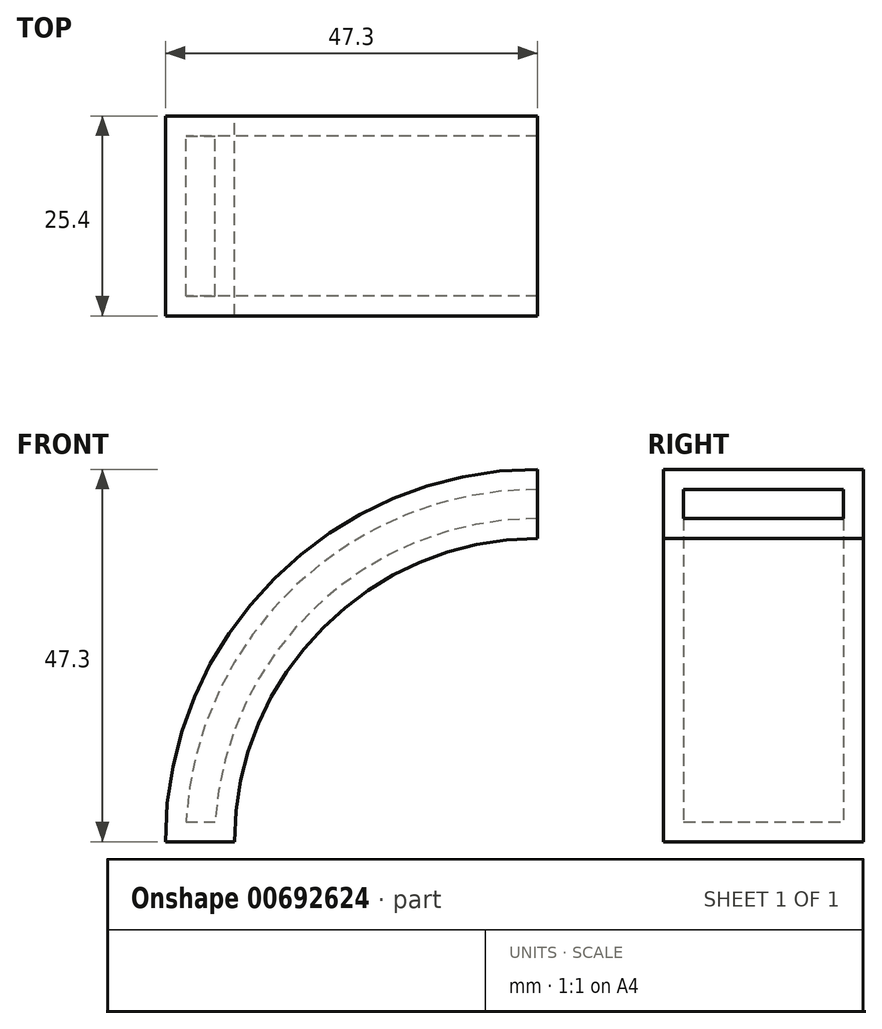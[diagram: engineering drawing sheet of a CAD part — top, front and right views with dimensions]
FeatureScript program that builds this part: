
annotation { "Feature Type Name" : "Feature", "Feature Type Description" : "" }
export const myFeature = defineFeature(function(context is Context, id is Id, definition is map)
    precondition{}
    {
        {
            var Q0;
            Q0=qCreatedBy(makeId("Front.planeOp"),FACE);
            var sketch = newSketch(context, id + "F0", { "sketchPlane" : qUnion([Q0])});
            skArc(sketch, "E0", {"start": v(0, 47.3) * mm, "mid": v(-33.45, 33.45) * mm, "end": v(-47.3, 0) * mm});
            skArc(sketch, "E1", {"start": v(0, 38.5) * mm, "mid": v(-27.23, 27.23) * mm, "end": v(-38.5, 0) * mm});
            skLineSegment(sketch, "E2", {"start": v(0, 47.3) * mm, "end": v(0, 38.5) * mm});
            skLineSegment(sketch, "E3", {"start": v(-47.3, 0) * mm, "end": v(-38.5, 0) * mm});
            skPoint(sketch, "E4.orphan", {"position": v(-58.88, 0) * mm});
            skPoint(sketch, "E5.orphan", {"position": v(0, 56.68) * mm});
            skSolve(sketch);
        }
        {
            var Q0;
            Q0=makeQuery(id+"F0.imprint","IMPRINT",FACE,{"disambiguationData":[TD([[makeQuery(id+"F0.imprint","IMPRINT",EDGE,{"derivedFrom":sQuery(id+"F0.wireOp",EDGE,"E0")}),1.0]])]});
            extrude(context, id + "F1", {"entities" : qUnion([Q0]), "depth" : 25.4 * mm, "offsetDistance" : 25.4 * mm});
        }
        {
            var Q0;
            Q0=makeQuery(id+"F1.opExtrude","SWEPT_FACE",FACE,{"disambiguationData":[OSD([sQuery(id+"F0.wireOp",EDGE,"E2")])]});
            shell(context, id + "F2", {"entities" : qUnion([Q0]), "thickness" : 2.54 * mm});
        }
    });
